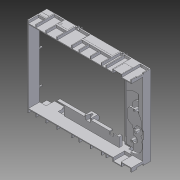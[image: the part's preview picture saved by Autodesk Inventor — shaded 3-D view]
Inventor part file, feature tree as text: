
AUTODESK INVENTOR PART (.ipt)
format: ipt  version: 2011 (Build 150239000, 239)  size: 536,064 bytes
history: native  units: in
note: dims shown in document units (in); Inventor stores cm internally (conversion verified against a paired STEP export)
features: extrude x2, sketch x2, other x1, imported_body x1
ambient origin geometry x8: Origin, YZ Plane, XZ Plane, XY Plane, X Axis, Y Axis, Z Axis, Center Point
feature tree (6):
  other  "Part5"
  imported_body  "Base1"
  extrude  "Extrusion1"  Depth=0.5906in TaperAngle=0.0deg
  extrude  "Extrusion2"  [1 undecoded]
  sketch  "Sketch1"  dims[d0=0.3937in d1=0.0in d2=0.5906in d3=0.0in]
  sketch  "Sketch2"  dims[d4=0.3937in d5=0.0in]
note: 1 required parameter value undecoded (feature->parameter linkage not recoverable at this tier; creation-order binding heuristic only, values carry confidence <= 0.55)
